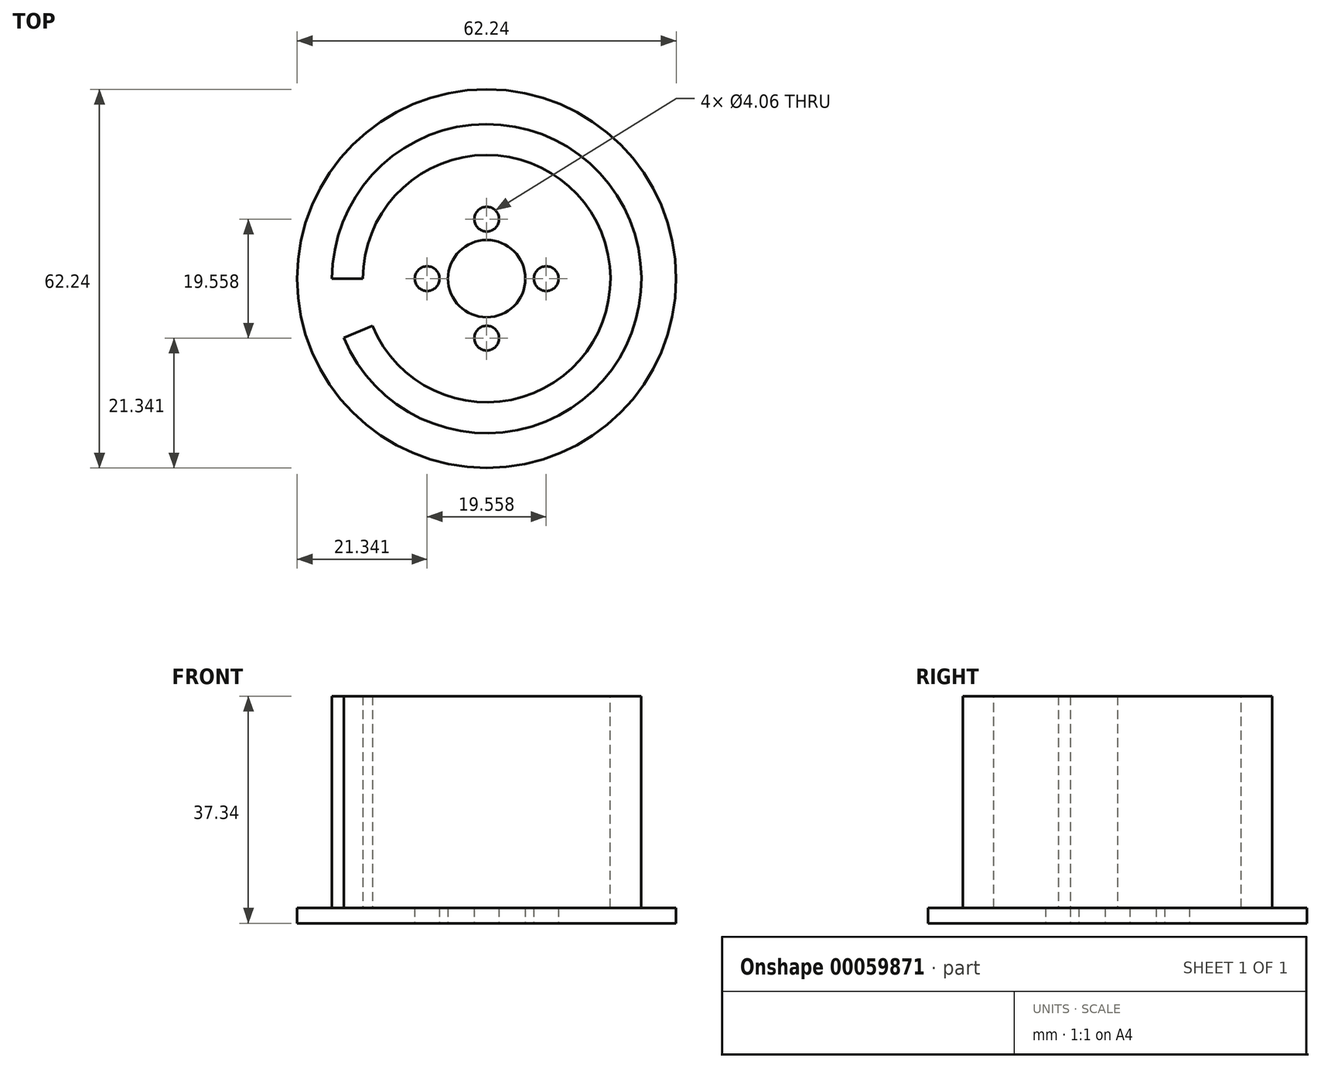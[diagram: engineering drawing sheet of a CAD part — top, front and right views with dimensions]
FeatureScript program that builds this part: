
annotation { "Feature Type Name" : "Feature", "Feature Type Description" : "" }
export const myFeature = defineFeature(function(context is Context, id is Id, definition is map)
    precondition{}
    {
        {
            var Q0;
            Q0=qCreatedBy(makeId("Front.planeOp"),FACE);
            var sketch = newSketch(context, id + "F0", { "sketchPlane" : qUnion([Q0])});
            skLineSegment(sketch, "E0", {"start": v(0, 0) * mm, "end": v(-31.12, 0) * mm});
            skLineSegment(sketch, "E1", {"start": v(0, 0) * mm, "end": v(31.12, 0) * mm});
            skLineSegment(sketch, "E2", {"start": v(31.12, 0) * mm, "end": v(31.12, 2.54) * mm});
            skLineSegment(sketch, "E3", {"start": v(31.12, 2.54) * mm, "end": v(25.4, 2.54) * mm});
            skLineSegment(sketch, "E4", {"start": v(25.4, 2.54) * mm, "end": v(25.4, 37.34) * mm});
            skLineSegment(sketch, "E5", {"start": v(25.4, 37.34) * mm, "end": v(31.12, 37.34) * mm});
            skLineSegment(sketch, "E6", {"start": v(31.11, 37.34) * mm, "end": v(31.11, 39.88) * mm});
            skLineSegment(sketch, "E7", {"start": v(31.12, 39.88) * mm, "end": v(-31.12, 39.88) * mm});
            skLineSegment(sketch, "E8", {"start": v(-31.12, 39.88) * mm, "end": v(-31.12, 37.34) * mm});
            skLineSegment(sketch, "E9", {"start": v(-31.12, 37.34) * mm, "end": v(-25.4, 37.34) * mm});
            skLineSegment(sketch, "E10", {"start": v(-25.4, 37.34) * mm, "end": v(-25.4, 2.54) * mm});
            skLineSegment(sketch, "E11", {"start": v(-25.4, 2.54) * mm, "end": v(-31.12, 2.54) * mm});
            skLineSegment(sketch, "E12", {"start": v(-31.12, 2.54) * mm, "end": v(-31.11, 0) * mm});
            skLineSegment(sketch, "E13", {"start": v(0, 39.88) * mm, "end": v(0, 0) * mm});
            skLineSegment(sketch, "E14", {"start": v(-25.4, 37.34) * mm, "end": v(-20.32, 37.34) * mm});
            skLineSegment(sketch, "E15", {"start": v(-20.32, 37.34) * mm, "end": v(-20.32, 2.54) * mm});
            skLineSegment(sketch, "E16", {"start": v(-20.32, 2.54) * mm, "end": v(-25.4, 2.54) * mm});
            skLineSegment(sketch, "E17", {"start": v(-20.32, 37.34) * mm, "end": v(0, 37.34) * mm});
            skLineSegment(sketch, "E18", {"start": v(-20.32, 2.54) * mm, "end": v(0, 2.54) * mm});
            skSolve(sketch);
        }
        {
            var Q0;
            Q0=makeQuery(id+"F0.imprint","IMPRINT",FACE,{"disambiguationData":[TD([[makeQuery(id+"F0.imprint","IMPRINT",EDGE,{"derivedFrom":sQuery(id+"F0.wireOp",EDGE,"E10")}),1.0]])]});
            var Q1;
            Q1=sQuery(id+"F0.wireOp",EDGE,"E13");
            revolve(context, id + "F1", {"entities" : qUnion([Q0]), "axis" : qUnion([Q1]), "revolveType" : RevolveType.ONE_DIRECTION, "angle" : 337.5 * degree});
        }
        {
            var Q0;
            {var subQ1=sQuery(id+"F0.wireOp",EDGE,"E0");Q0=makeQuery(id+"F0.imprint","IMPRINT",FACE,{"disambiguationData":[TD([[makeQuery(id+"F0.imprint","IMPRINT",EDGE,{"derivedFrom":subQ1}),-1.0]])]});}
            var Q1;
            Q1=sQuery(id+"F0.wireOp",EDGE,"E13");
            revolve(context, id + "F2", {"operationType" : NewBodyOperationType.ADD, "entities" : qUnion([Q0]), "axis" : qUnion([Q1]), "revolveType" : RevolveType.FULL});
        }
        {
            var Q0;
            Q0=makeQuery(id+"F2.opRevolve","SWEPT_FACE",FACE,{"disambiguationData":[OSD([sQuery(id+"F0.wireOp",EDGE,"E0")])]});
            var sketch = newSketch(context, id + "F3", { "sketchPlane" : qUnion([Q0])});
            skCircle(sketch, "E19", {"center": v(0, 0) * mm, "radius": 6.35 * mm});
            skLineSegment(sketch, "E20", {"start": v(0, 0) * mm, "end": v(0, 9.78) * mm});
            skLineSegment(sketch, "E21", {"start": v(0, 0) * mm, "end": v(9.78, 0) * mm});
            skLineSegment(sketch, "E22", {"start": v(0, 0) * mm, "end": v(0, -9.78) * mm});
            skLineSegment(sketch, "E23", {"start": v(0, 0) * mm, "end": v(-9.78, 0) * mm});
            skCircle(sketch, "E24", {"center": v(0, 9.78) * mm, "radius": 2.03 * mm});
            skCircle(sketch, "E25", {"center": v(9.78, 0) * mm, "radius": 2.03 * mm});
            skCircle(sketch, "E26", {"center": v(0, -9.78) * mm, "radius": 2.03 * mm});
            skCircle(sketch, "E27", {"center": v(-9.78, 0) * mm, "radius": 2.03 * mm});
            skSolve(sketch);
        }
        {
            var Q0;
            Q0 = qSketchRegion(id + "F3", true);
            extrude(context, id + "F4", {"entities" : qUnion([Q0]), "operationType" : NewBodyOperationType.REMOVE, "oppositeDirection" : true, "depth" : 10.6 * mm});
        }
    });
